# Revit family: KDW010085
name_source: partatom
category: Plumbing Fixtures
revit_build: Autodesk Revit 2015 (Build: 20140606_1530(x64)
units: mm (PartAtom-declared; Revit-internal decimal feet)

## types (1)
- CENTRO UNTERBAUWASCHTISCH 3059 380x610
    BIMobject category = Basins
    Brand url = http://www.kaldewei.com
    Color = https://www.kaldewei.co.uk
    ColourOptions = https://www.kaldewei.co.uk
    Design country = Germany
    Durability = https://www.kaldewei.de
    Edition number = 1
    Features = https://www.kaldewei.co.uk
    Finish = https://n
    Finition = Kaldewei
    HasGrabHandles = https://www.kaldewei.co.uk
    IFC Classification = Furnishing Element
    IfcExportAs = WASHHANDBASIN
    IfcExportType = IfcSanitaryTerminalType
    IntegralAccessories = https://www.kaldewei.co.uk
    Manufacturer = Kaldewei
    Manufacturer country = Germany
    ManufacturerCountry = GERMANY
    ManufacturerName = KALDEWEI
    ManufacturerURL = https://www.kaldewei.com
    Material = steel enamel
    Material main = Steel
    Material secondary = Enamel
    Metal = Chrome
    Model = CENTROUNTERBAUWASCHTISCH
    NBS Reference Code = 35-65-70-94
    NBS Reference Description = Wash Basin Systems
    Name = CENTRO Undercounter washbasin
    Nominal height = 610 cm
    Nominal width = 380 cm
    NominalLength = 610
    ObjectName = CENTRO Undercounter washbasin 380x610
    ObjectNorm = EN 14688EU DECLARATION OF PERFORMANCE(https://www.kaldewei.de
    ObjectPicture = https://www.kaldewei.co.uk
    ObjectURL = https://www.kaldewei.co.uk
    Polantis code = KDW010085
    Product Guid = c0de1639-01b4-4ee2-8bd2-3d6fe922da2c
    Product SKU = 3059
    Product certification = https://www.kaldewei.co.uk
    Product data url = https://bimobject.com
    Product family = CENTRO
    Product group = Washbasin
    Product url = https://www.kaldewei.co.uk
    ProductInformation = Model No.3059: Fusion of minimalism and simple elegance- luxurious look – integrates perfectly both in modern and traditional bathroom settings - circle taken as the basic shape echoes in the perfectly integrated enamelled waste- washbasin surround with ample space for individual accessories- matching counterpart to the Centro bath- designed by Anke Salomon
    QR code = http://bimobject.com
    Revision = 1
    SerialNumber = 3059
    Shape = Undercounter
    Size = 380x610
    SupportFrame = https://www.kaldewei.co.uk
    Sustainability = https://kaldewei-fa.secure.footprint.net
    Technical description = https://www.kaldewei.co.uk
    TechnicalDataURL = https://kaldewei.typo-live.web-factory.de
    Type Comments = CENTRO UNTERBAUWASCHTISCH 3059 380x610
    UNSPSC Code = 301815
    UNSPSCCode = 30181504
    UNSPSCNames = Sinks
    URL = https://www.kaldewei.co.uk
    Uniclass 1.4 Code = L7212
    Uniclass 1.4 Description = Washbasins
    Uniclass 2.0 Code = SS-35-65-70-94
    Uniclass 2.0 Description = Wash Basin Systems
    Uniclass 2015 = Pr_40_20_96
    Version = 4
    WarrantyDurationParts = 30
    WarrantyDurationUnit = Year
    WarrantyStartDate = https://www.kaldewei.co.uk
    Weight = 6,4
    Weight Net (Kg) = 6.4

## geometry (parser evidence)
native form markers: Sweep x7
no freeform markers — native parametric forms only
